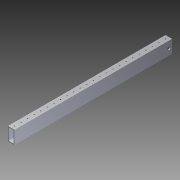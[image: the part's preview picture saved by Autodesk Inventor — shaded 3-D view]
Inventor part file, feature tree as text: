
AUTODESK INVENTOR PART (.ipt)
format: ipt  version: 2014 SP1 (Build 180222100, 222)  size: 741,376 bytes
history: native  units: in
note: dims shown in document units (in); Inventor stores cm internally (conversion verified against a paired STEP export)
features: other x2, extrude x2, sketch x2, imported_body x1
ambient origin geometry x8: Origin, YZ Plane, XZ Plane, XY Plane, X Axis, Y Axis, Z Axis, Center Point
bodies: Body1 (feature_tree)
feature tree (7):
  other  "Cut-Extrude2"
  other  "2x1 Tube1"
  extrude  "Extrusion1"  Depth=0.5in
  extrude  "Extrusion2"  Depth=1.0in TaperAngle=0.0deg
  imported_body  "Base1"
  sketch  "Sketch1"  dims[d0=35.0in d1=0.0in d2=0.5in]
  sketch  "Sketch2"  dims[d3=0.5in d4=1.0in d5=0.0in]
